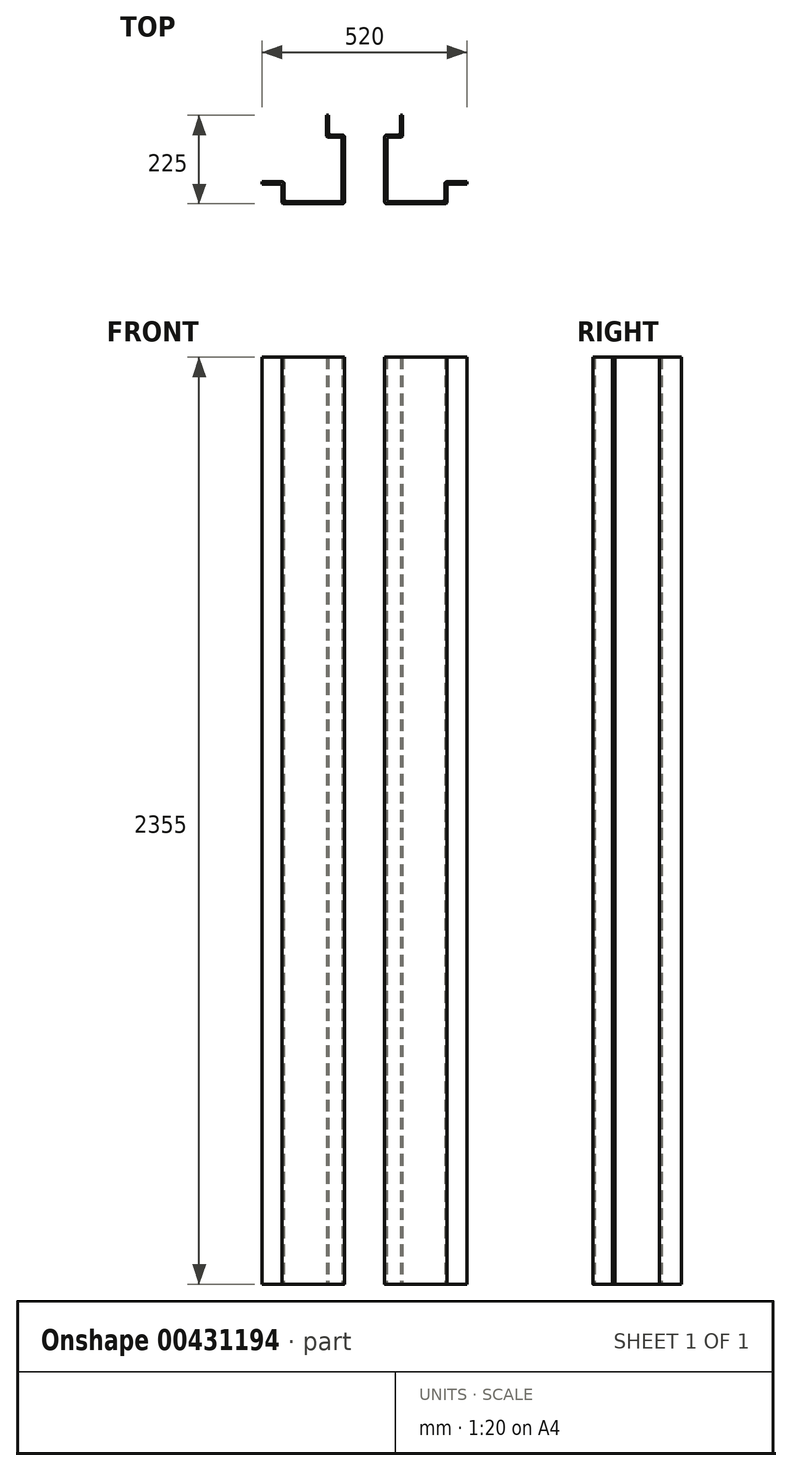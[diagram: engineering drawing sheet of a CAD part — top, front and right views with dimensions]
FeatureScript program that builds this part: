
annotation { "Feature Type Name" : "Feature", "Feature Type Description" : "" }
export const myFeature = defineFeature(function(context is Context, id is Id, definition is map)
    precondition{}
    {
        {
            var Q0;
            Q0=qCreatedBy(makeId("Top.planeOp"),FACE);
            var sketch = newSketch(context, id + "F0", { "sketchPlane" : qUnion([Q0])});
            skLineSegment(sketch, "E0", {"start": v(-91, 0) * mm, "end": v(-91, -44) * mm});
            skLineSegment(sketch, "E1", {"start": v(-85, -50) * mm, "end": v(-57, -50) * mm});
            skLineSegment(sketch, "E2", {"start": v(-51, -56) * mm, "end": v(-51, -219) * mm});
            skLineSegment(sketch, "E3", {"start": v(-57, -225) * mm, "end": v(-204, -225) * mm});
            skLineSegment(sketch, "E4", {"start": v(-210, -219) * mm, "end": v(-210, -181) * mm});
            skLineSegment(sketch, "E5", {"start": v(-216, -175) * mm, "end": v(-260, -175) * mm});
            skLineSegment(sketch, "E6.0", {"start": v(-97, 0) * mm, "end": v(-97, -50) * mm});
            skLineSegment(sketch, "E7.0", {"start": v(-91, -56) * mm, "end": v(-63, -56) * mm});
            skLineSegment(sketch, "E8.0", {"start": v(-57, -62) * mm, "end": v(-57, -213) * mm});
            skLineSegment(sketch, "E9.0", {"start": v(-63, -219) * mm, "end": v(-198, -219) * mm});
            skLineSegment(sketch, "E10.0", {"start": v(-204, -213) * mm, "end": v(-204, -175) * mm});
            skLineSegment(sketch, "E11.0", {"start": v(-210, -169) * mm, "end": v(-260, -169) * mm});
            skLineSegment(sketch, "E12", {"start": v(-97, 0) * mm, "end": v(-91, 0) * mm});
            skLineSegment(sketch, "E13", {"start": v(-260, -175) * mm, "end": v(-260, -169) * mm});
            skPoint(sketch, "E14.visualSharp", {"position": v(-97, -56) * mm});
            skArc(sketch, "E14.filletArc", {"start": v(-97, -50) * mm, "mid": v(-95.24, -54.24) * mm, "end": v(-91, -56) * mm});
            skArc(sketch, "E15.filletArc", {"start": v(-91, -44) * mm, "mid": v(-89.24, -48.24) * mm, "end": v(-85, -50) * mm});
            skPoint(sketch, "E16.visualSharp", {"position": v(-51, -50) * mm});
            skArc(sketch, "E16.filletArc", {"start": v(-51, -56) * mm, "mid": v(-52.76, -51.76) * mm, "end": v(-57, -50) * mm});
            skArc(sketch, "E17.filletArc", {"start": v(-57, -62) * mm, "mid": v(-58.76, -57.76) * mm, "end": v(-63, -56) * mm});
            skPoint(sketch, "E18.visualSharp", {"position": v(-57, -219) * mm});
            skArc(sketch, "E18.filletArc", {"start": v(-63, -219) * mm, "mid": v(-58.76, -217.24) * mm, "end": v(-57, -213) * mm});
            skPoint(sketch, "E19.visualSharp", {"position": v(-51, -225) * mm});
            skArc(sketch, "E19.filletArc", {"start": v(-57, -225) * mm, "mid": v(-52.76, -223.24) * mm, "end": v(-51, -219) * mm});
            skPoint(sketch, "E20.visualSharp", {"position": v(-204, -219) * mm});
            skArc(sketch, "E20.filletArc", {"start": v(-204, -213) * mm, "mid": v(-202.24, -217.24) * mm, "end": v(-198, -219) * mm});
            skPoint(sketch, "E21.visualSharp", {"position": v(-210, -225) * mm});
            skArc(sketch, "E21.filletArc", {"start": v(-210, -219) * mm, "mid": v(-208.24, -223.24) * mm, "end": v(-204, -225) * mm});
            skPoint(sketch, "E22.visualSharp", {"position": v(-210, -175) * mm});
            skArc(sketch, "E22.filletArc", {"start": v(-210, -181) * mm, "mid": v(-211.76, -176.76) * mm, "end": v(-216, -175) * mm});
            skPoint(sketch, "E23.visualSharp", {"position": v(-204, -169) * mm});
            skArc(sketch, "E23.filletArc", {"start": v(-204, -175) * mm, "mid": v(-205.76, -170.76) * mm, "end": v(-210, -169) * mm});
            skSolve(sketch);
        }
        {
            var Q0;
            Q0=makeQuery(id+"F0.imprint","IMPRINT",FACE,{"disambiguationData":[TD([[makeQuery(id+"F0.imprint","IMPRINT",EDGE,{"derivedFrom":sQuery(id+"F0.wireOp",EDGE,"E0")}),-1.0]])]});
            extrude(context, id + "F1", {"entities" : qUnion([Q0]), "depth" : 2355 * mm});
        }
        {
            var Q0;
            Q0=makeQuery(id+"F1.opExtrude","SWEPT_BODY",BODY,{"disambiguationData":[OSD([sQuery(id+"F0.wireOp",EDGE,"E0"),sQuery(id+"F0.wireOp",EDGE,"E1"),sQuery(id+"F0.wireOp",EDGE,"E2"),sQuery(id+"F0.wireOp",EDGE,"E3"),sQuery(id+"F0.wireOp",EDGE,"E4"),sQuery(id+"F0.wireOp",EDGE,"E5"),sQuery(id+"F0.wireOp",EDGE,"E6.0"),sQuery(id+"F0.wireOp",EDGE,"E7.0"),sQuery(id+"F0.wireOp",EDGE,"E8.0"),sQuery(id+"F0.wireOp",EDGE,"E9.0"),sQuery(id+"F0.wireOp",EDGE,"E10.0"),sQuery(id+"F0.wireOp",EDGE,"E11.0"),sQuery(id+"F0.wireOp",EDGE,"E12"),sQuery(id+"F0.wireOp",EDGE,"E13"),sQuery(id+"F0.wireOp",EDGE,"E14.filletArc"),sQuery(id+"F0.wireOp",EDGE,"E15.filletArc"),sQuery(id+"F0.wireOp",EDGE,"E16.filletArc"),sQuery(id+"F0.wireOp",EDGE,"E17.filletArc"),sQuery(id+"F0.wireOp",EDGE,"E18.filletArc"),sQuery(id+"F0.wireOp",EDGE,"E19.filletArc"),sQuery(id+"F0.wireOp",EDGE,"E20.filletArc"),sQuery(id+"F0.wireOp",EDGE,"E21.filletArc"),sQuery(id+"F0.wireOp",EDGE,"E22.filletArc"),sQuery(id+"F0.wireOp",EDGE,"E23.filletArc")])]});
            var Q1;
            Q1=qCreatedBy(makeId("Right.planeOp"),FACE);
            mirror(context, id + "F2", {"entities" : qUnion([Q0]), "mirrorPlane" : qUnion([Q1])});
        }
    });
